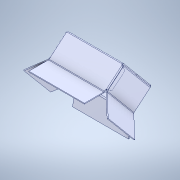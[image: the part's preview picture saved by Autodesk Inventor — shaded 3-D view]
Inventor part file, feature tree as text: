
AUTODESK INVENTOR PART (.ipt)
format: ipt  version: 2022 (Build 260153000, 153)  size: 215,552 bytes
history: imported  units: mm
features: other x1, sketch x1, imported_body x1
ambient origin geometry x8: Origin, YZ Plane, XZ Plane, XY Plane, X Axis, Y Axis, Z Axis, Center Point
bodies: Body1 (imported_parasolid)
feature tree (3):
  other  "Sólido1"
  sketch  "Sketched Bend45"
  imported_body  NMx_Import_Brep_tag  [imported B-rep: ~28 faces, bbox_mm=[389.287611, 323.202923, 203.694785]]
